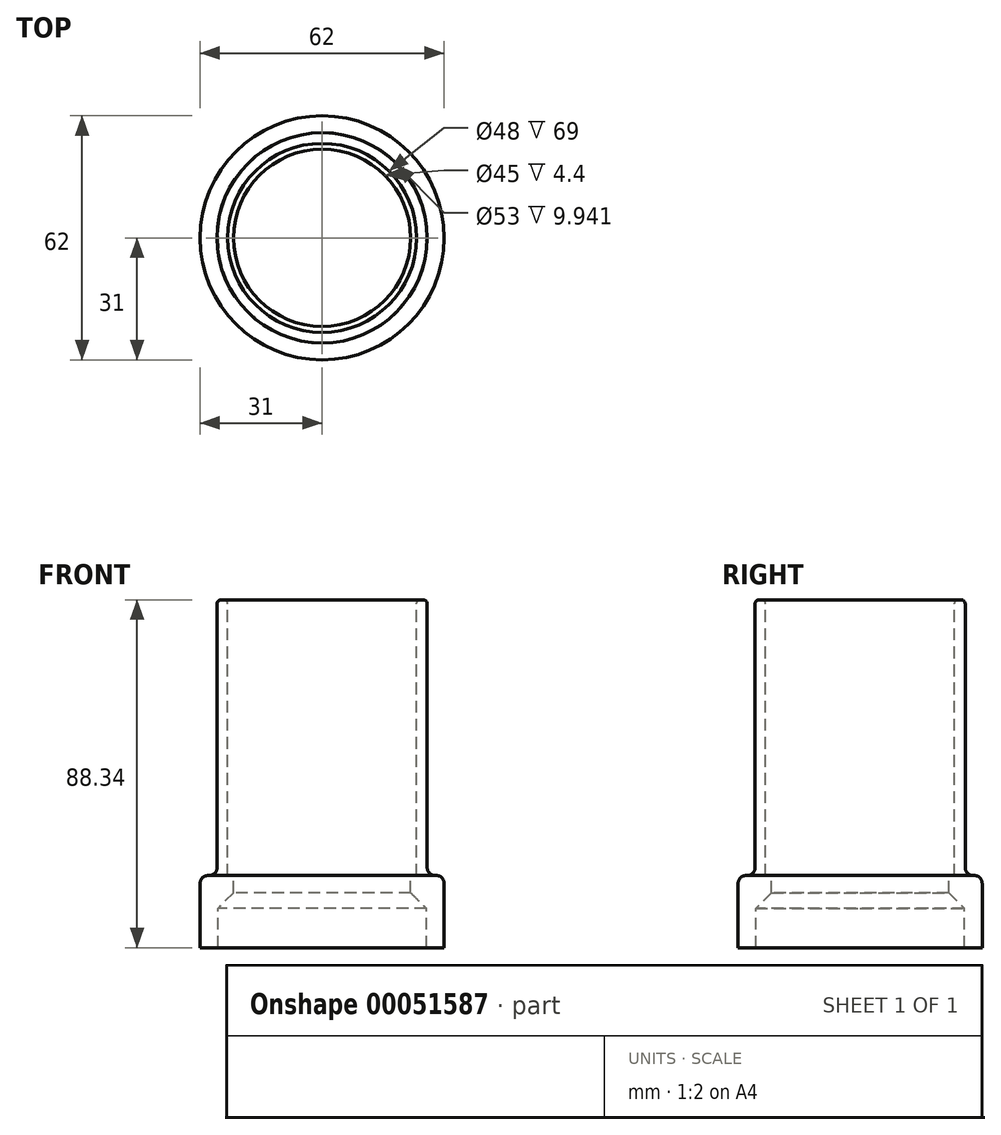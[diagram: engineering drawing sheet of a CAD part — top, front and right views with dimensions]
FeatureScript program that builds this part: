
annotation { "Feature Type Name" : "Feature", "Feature Type Description" : "" }
export const myFeature = defineFeature(function(context is Context, id is Id, definition is map)
    precondition{}
    {
        {
            var Q0;
            Q0=qCreatedBy(makeId("Front.planeOp"),FACE);
            var sketch = newSketch(context, id + "F0", { "sketchPlane" : qUnion([Q0])});
            skLineSegment(sketch, "E0", {"start": v(0, 41.02) * mm, "end": v(0, -30.3) * mm});
            skLineSegment(sketch, "E1", {"start": v(24, 80) * mm, "end": v(24, 10) * mm});
            skLineSegment(sketch, "E2", {"start": v(24, 10) * mm, "end": v(22.5, 10) * mm});
            skLineSegment(sketch, "E3", {"start": v(22.5, 10) * mm, "end": v(22.5, 5.6) * mm});
            skLineSegment(sketch, "E4", {"start": v(22.5, 5.6) * mm, "end": v(26.5, 1.6) * mm});
            skLineSegment(sketch, "E5", {"start": v(26.5, 1.6) * mm, "end": v(26.5, -8.33) * mm});
            skLineSegment(sketch, "E6", {"start": v(26.5, -8.33) * mm, "end": v(31, -8.33) * mm});
            skLineSegment(sketch, "E7", {"start": v(31, -8.33) * mm, "end": v(31, 10) * mm});
            skLineSegment(sketch, "E8", {"start": v(31, 10) * mm, "end": v(26.7, 10) * mm});
            skLineSegment(sketch, "E9", {"start": v(26.7, 10) * mm, "end": v(26.7, 80) * mm});
            skLineSegment(sketch, "E10", {"start": v(26.7, 80) * mm, "end": v(24, 80) * mm});
            skSolve(sketch);
        }
        {
            var Q0;
            Q0=makeQuery(id+"F0.imprint","IMPRINT",FACE,{"disambiguationData":[TD([[makeQuery(id+"F0.imprint","IMPRINT",EDGE,{"derivedFrom":sQuery(id+"F0.wireOp",EDGE,"E1")}),1.0]])]});
            var Q1;
            Q1=sQuery(id+"F0.wireOp",EDGE,"E0");
            revolve(context, id + "F1", {"entities" : qUnion([Q0]), "axis" : qUnion([Q1]), "revolveType" : RevolveType.FULL});
        }
        {
            var Q0;
            Q0=makeQuery(id+"F1.opRevolve","SWEPT_EDGE",EDGE,{"disambiguationData":[OSD([sQuery(id+"F0.wireOp",EDGE,"E8"),sQuery(id+"F0.wireOp",EDGE,"E9")])]});
            var Q1;
            Q1=makeQuery(id+"F1.opRevolve","SWEPT_EDGE",EDGE,{"disambiguationData":[OSD([sQuery(id+"F0.wireOp",EDGE,"E7"),sQuery(id+"F0.wireOp",EDGE,"E8")])]});
            fillet(context, id + "F2", {"entities" : qUnion([Q0, Q1]), "radius" : 2 * mm, "tangentPropagation" : true, "allowEdgeOverflow" : false});
        }
        {
            var Q0;
            Q0=makeQuery(id+"F1.opRevolve","SWEPT_EDGE",EDGE,{"disambiguationData":[OSD([sQuery(id+"F0.wireOp",EDGE,"E1"),sQuery(id+"F0.wireOp",EDGE,"E10")])]});
            var Q1;
            Q1=makeQuery(id+"F1.opRevolve","SWEPT_EDGE",EDGE,{"disambiguationData":[OSD([sQuery(id+"F0.wireOp",EDGE,"E9"),sQuery(id+"F0.wireOp",EDGE,"E10")])]});
            fillet(context, id + "F3", {"entities" : qUnion([Q0, Q1]), "radius" : 1 * mm, "tangentPropagation" : true, "allowEdgeOverflow" : false});
        }
    });
